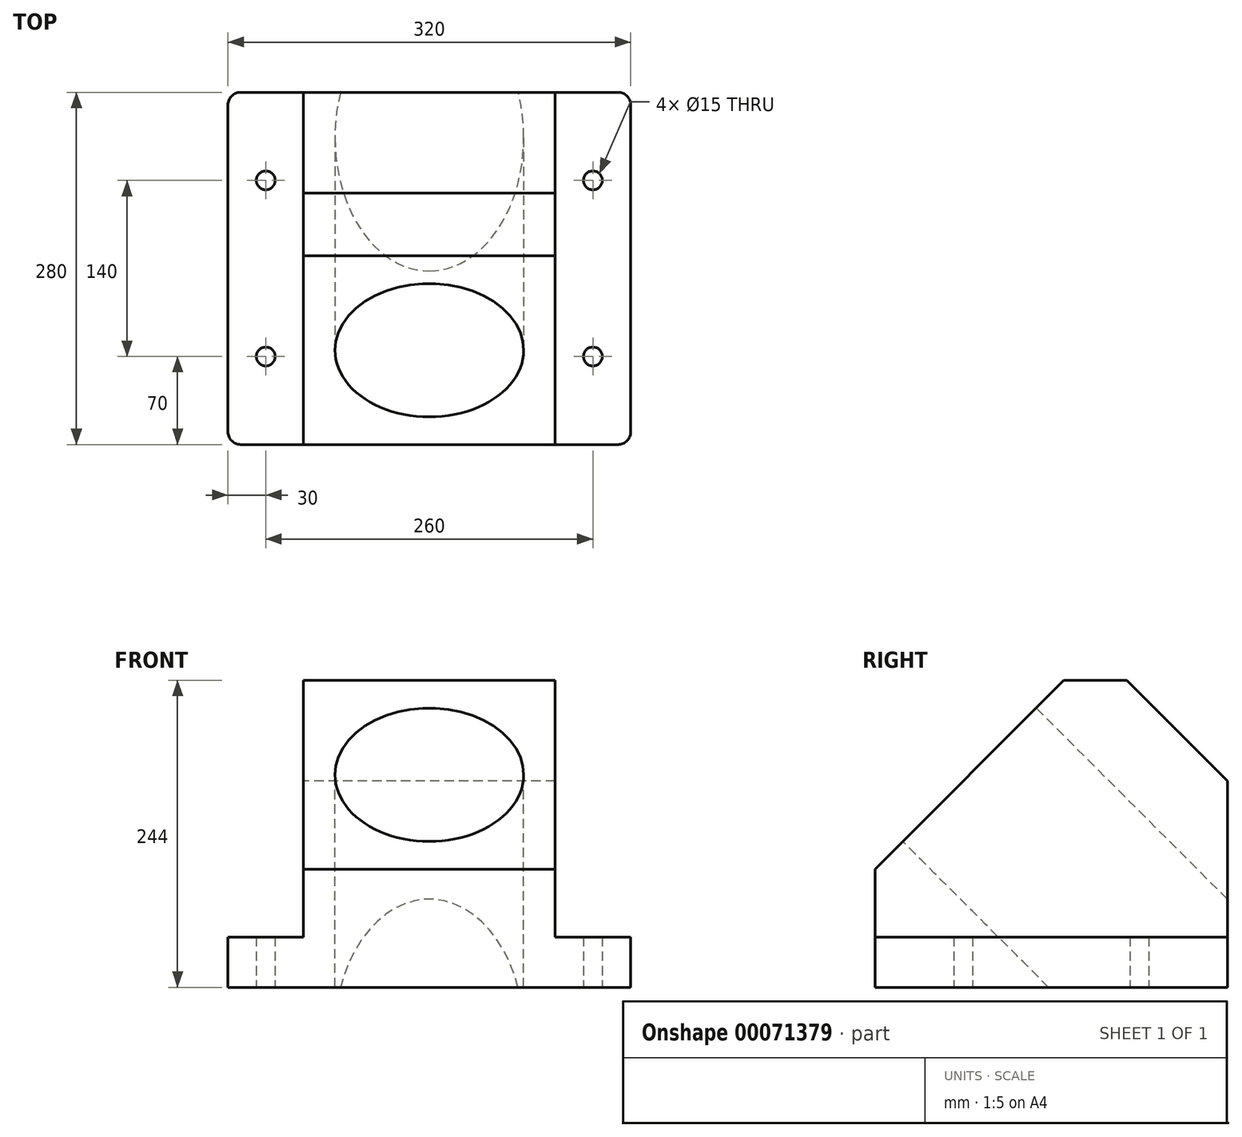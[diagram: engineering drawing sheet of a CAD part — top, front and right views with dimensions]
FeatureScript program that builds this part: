
annotation { "Feature Type Name" : "Feature", "Feature Type Description" : "" }
export const myFeature = defineFeature(function(context is Context, id is Id, definition is map)
    precondition{}
    {
        {
            var Q0;
            Q0=qCreatedBy(makeId("Right.planeOp"),FACE);
            var sketch = newSketch(context, id + "F0", { "sketchPlane" : qUnion([Q0])});
            skLineSegment(sketch, "E0.bottom", {"start": v(-140, 0) * mm, "end": v(140, 0) * mm});
            skLineSegment(sketch, "E0.top", {"start": v(-140, 94) * mm, "end": v(140, 94) * mm, "construction": true});
            skLineSegment(sketch, "E0.left", {"start": v(-140, 0) * mm, "end": v(-140, 94) * mm});
            skLineSegment(sketch, "E0.right", {"start": v(140, 0) * mm, "end": v(140, 94) * mm});
            skLineSegment(sketch, "E1", {"start": v(-140, 0) * mm, "end": v(0, 0) * mm});
            skLineSegment(sketch, "E2", {"start": v(0, 0) * mm, "end": v(140, 0) * mm});
            skLineSegment(sketch, "E3", {"start": v(140, 94) * mm, "end": v(140, 164) * mm});
            skLineSegment(sketch, "E4", {"start": v(140, 164) * mm, "end": v(-140, 94) * mm, "construction": true});
            skLineSegment(sketch, "E5", {"start": v(10, 244) * mm, "end": v(60, 244) * mm});
            skLineSegment(sketch, "E6", {"start": v(60, 244) * mm, "end": v(140, 164) * mm});
            skLineSegment(sketch, "E7", {"start": v(10, 244) * mm, "end": v(-140, 94) * mm});
            skSolve(sketch);
        }
        {
            var Q0;
            Q0=makeQuery(id+"F0.imprint","IMPRINT",FACE,{"disambiguationData":[TD([[makeQuery(id+"F0.imprint","IMPRINT",EDGE,{"derivedFrom":sQuery(id+"F0.wireOp",EDGE,"E0.left")}),-1.0]])]});
            extrude(context, id + "F1", {"entities" : qUnion([Q0]), "depth" : 200 * mm, "symmetric" : true});
        }
        {
            var Q0;
            Q0=makeQuery(id+"F1.opExtrude","SWEPT_FACE",FACE,{"disambiguationData":[OSD([sQuery(id+"F0.wireOp",EDGE,"E7")])]});
            var sketch = newSketch(context, id + "F2", { "sketchPlane" : qUnion([Q0])});
            skLineSegment(sketch, "E8", {"start": v(-100, -32.53) * mm, "end": v(0, 73.54) * mm, "construction": true});
            skLineSegment(sketch, "E9", {"start": v(0, 73.54) * mm, "end": v(100, -32.53) * mm, "construction": true});
            skLineSegment(sketch, "E10", {"start": v(100, 179.6) * mm, "end": v(0, 73.54) * mm, "construction": true});
            skLineSegment(sketch, "E11", {"start": v(-100, 179.6) * mm, "end": v(0, 73.54) * mm, "construction": true});
            skCircle(sketch, "E12", {"center": v(0, 73.54) * mm, "radius": 75 * mm});
            skSolve(sketch);
        }
        {
            var Q0;
            Q0=qCreatedBy(makeId("Top.planeOp"),FACE);
            var sketch = newSketch(context, id + "F3", { "sketchPlane" : qUnion([Q0])});
            skLineSegment(sketch, "E13.bottom", {"start": v(150, -140) * mm, "end": v(-150, -140) * mm});
            skLineSegment(sketch, "E13.top", {"start": v(150, 140) * mm, "end": v(-150, 140) * mm});
            skLineSegment(sketch, "E13.left", {"start": v(160, -130) * mm, "end": v(160, 130) * mm});
            skLineSegment(sketch, "E13.right", {"start": v(-160, -130) * mm, "end": v(-160, 130) * mm});
            skPoint(sketch, "E13.middle", {"position": v(0, 0) * mm});
            skPoint(sketch, "E14.visualSharp", {"position": v(-160, 140) * mm});
            skArc(sketch, "E14.filletArc", {"start": v(-150, 140) * mm, "mid": v(-157.07, 137.07) * mm, "end": v(-160, 130) * mm});
            skPoint(sketch, "E15.visualSharp", {"position": v(160, 140) * mm});
            skArc(sketch, "E15.filletArc", {"start": v(160, 130) * mm, "mid": v(157.07, 137.07) * mm, "end": v(150, 140) * mm});
            skPoint(sketch, "E16.visualSharp", {"position": v(160, -140) * mm});
            skArc(sketch, "E16.filletArc", {"start": v(150, -140) * mm, "mid": v(157.07, -137.07) * mm, "end": v(160, -130) * mm});
            skPoint(sketch, "E17.visualSharp", {"position": v(-160, -140) * mm});
            skArc(sketch, "E17.filletArc", {"start": v(-160, -130) * mm, "mid": v(-157.07, -137.07) * mm, "end": v(-150, -140) * mm});
            skLineSegment(sketch, "E18.bottom", {"start": v(130, -70) * mm, "end": v(-130, -70) * mm, "construction": true});
            skLineSegment(sketch, "E18.top", {"start": v(130, 70) * mm, "end": v(-130, 70) * mm, "construction": true});
            skLineSegment(sketch, "E18.left", {"start": v(130, -70) * mm, "end": v(130, 70) * mm, "construction": true});
            skLineSegment(sketch, "E18.right", {"start": v(-130, -70) * mm, "end": v(-130, 70) * mm, "construction": true});
            skCircle(sketch, "E19", {"center": v(130, 70) * mm, "radius": 7.5 * mm});
            skCircle(sketch, "E20", {"center": v(130, -70) * mm, "radius": 7.5 * mm});
            skCircle(sketch, "E21", {"center": v(-130, -70) * mm, "radius": 7.5 * mm});
            skCircle(sketch, "E22", {"center": v(-130, 70) * mm, "radius": 7.5 * mm});
            skSolve(sketch);
        }
        {
            var Q0;
            Q0=makeQuery(id+"F3.imprint","IMPRINT",FACE,{"disambiguationData":[TD([[makeQuery(id+"F3.imprint","IMPRINT",EDGE,{"derivedFrom":sQuery(id+"F3.wireOp",EDGE,"E13.bottom")}),-1.0]])]});
            extrude(context, id + "F4", {"entities" : qUnion([Q0]), "operationType" : NewBodyOperationType.ADD, "depth" : 40 * mm});
        }
        {
            var Q0;
            Q0=makeQuery(id+"F2.imprint","IMPRINT",FACE,{"disambiguationData":[TD([[makeQuery(id+"F2.imprint","IMPRINT",EDGE,{"derivedFrom":sQuery(id+"F2.wireOp",EDGE,"E12")}),1.0]])]});
            extrude(context, id + "F5", {"entities" : qUnion([Q0]), "operationType" : NewBodyOperationType.REMOVE, "oppositeDirection" : true, "depth" : 1000 * mm});
        }
    });
